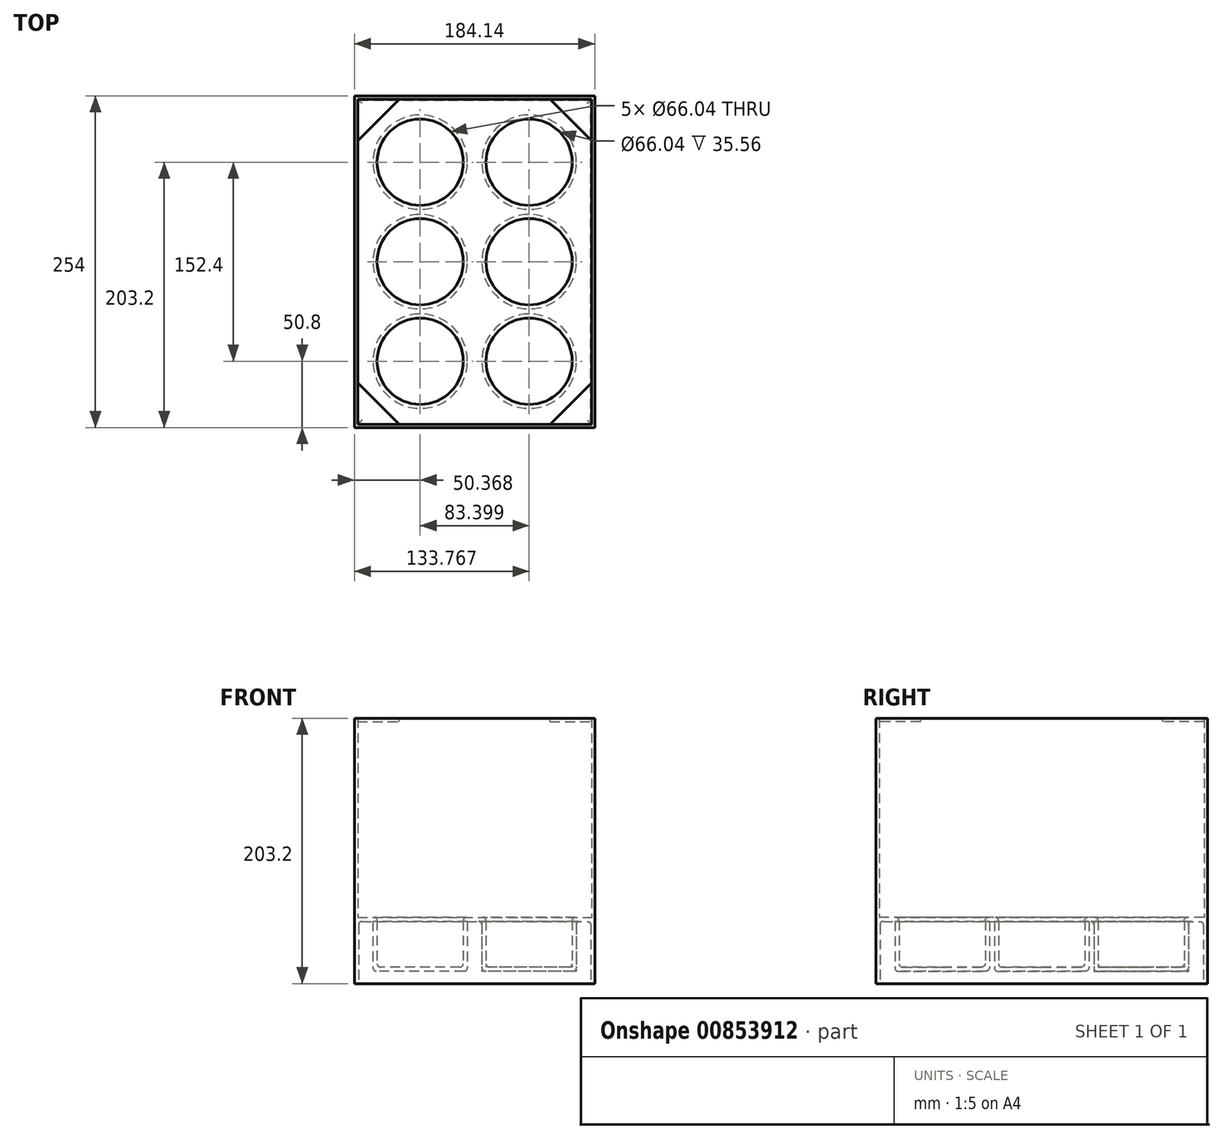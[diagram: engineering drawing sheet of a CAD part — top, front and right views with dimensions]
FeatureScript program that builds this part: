
annotation { "Feature Type Name" : "Feature", "Feature Type Description" : "" }
export const myFeature = defineFeature(function(context is Context, id is Id, definition is map)
    precondition{}
    {
        {
            var Q0;
            Q0=qCreatedBy(makeId("Top.planeOp"),FACE);
            var sketch = newSketch(context, id + "F0", { "sketchPlane" : qUnion([Q0])});
            skLineSegment(sketch, "E0.bottom", {"start": v(0, 0) * mm, "end": v(184.14, 0) * mm});
            skLineSegment(sketch, "E0.top", {"start": v(0, 254) * mm, "end": v(184.14, 254) * mm});
            skLineSegment(sketch, "E0.left", {"start": v(0, 0) * mm, "end": v(0, 254) * mm});
            skLineSegment(sketch, "E0.right", {"start": v(184.14, 0) * mm, "end": v(184.14, 254) * mm});
            skSolve(sketch);
        }
        {
            var Q0;
            Q0=makeQuery(id+"F0.imprint","IMPRINT",FACE,{"disambiguationData":[TD([[makeQuery(id+"F0.imprint","IMPRINT",EDGE,{"derivedFrom":sQuery(id+"F0.wireOp",EDGE,"E0.bottom")}),1.0]])]});
            extrude(context, id + "F1", {"entities" : qUnion([Q0]), "depth" : 12.7 * mm, "offsetDistance" : 25.4 * mm});
        }
        {
            var Q0;
            Q0=makeQuery(id+"F1.opExtrude","CAP_FACE",FACE,{"disambiguationData":[OSD([sQuery(id+"F0.wireOp",EDGE,"E0.bottom"),sQuery(id+"F0.wireOp",EDGE,"E0.top"),sQuery(id+"F0.wireOp",EDGE,"E0.left"),sQuery(id+"F0.wireOp",EDGE,"E0.right")])],"isStart":false});
            var sketch = newSketch(context, id + "F2", { "sketchPlane" : qUnion([Q0])});
            skCircle(sketch, "E1", {"center": v(50.37, 50.8) * mm, "radius": 33.02 * mm});
            skCircle(sketch, "E2", {"center": v(133.77, 50.8) * mm, "radius": 33.02 * mm});
            skCircle(sketch, "E3", {"center": v(50.37, 127) * mm, "radius": 33.02 * mm});
            skCircle(sketch, "E4", {"center": v(133.77, 127) * mm, "radius": 33.02 * mm});
            skCircle(sketch, "E5", {"center": v(50.37, 203.2) * mm, "radius": 33.02 * mm});
            skCircle(sketch, "E6", {"center": v(133.77, 203.2) * mm, "radius": 33.02 * mm});
            skSolve(sketch);
        }
        {
            var Q0;
            Q0=makeQuery(id+"F2.imprint","IMPRINT",FACE,{"disambiguationData":[TD([[makeQuery(id+"F2.imprint","IMPRINT",EDGE,{"derivedFrom":sQuery(id+"F2.wireOp",EDGE,"E1")}),-1.0]])]});
            extrude(context, id + "F3", {"entities" : qUnion([Q0]), "operationType" : NewBodyOperationType.ADD, "depth" : 38.1 * mm, "offsetDistance" : 25.4 * mm});
        }
        {
            var Q0;
            Q0=makeQuery(id+"F1.opExtrude","CAP_FACE",FACE,{"disambiguationData":[OSD([sQuery(id+"F0.wireOp",EDGE,"E0.bottom"),sQuery(id+"F0.wireOp",EDGE,"E0.top"),sQuery(id+"F0.wireOp",EDGE,"E0.left"),sQuery(id+"F0.wireOp",EDGE,"E0.right")])],"isStart":true});
            shell(context, id + "F4", {"entities" : qUnion([Q0]), "thickness" : 3.17 * mm});
        }
        {
            var Q0;
            Q0=makeQuery(id+"F3.opExtrude","CAP_EDGE",EDGE,{"disambiguationData":[OSD([sQuery(id+"F2.wireOp",EDGE,"E4")])],"isStart":true});
            var Q1;
            Q1=makeQuery(id+"F3.opExtrude","CAP_EDGE",EDGE,{"disambiguationData":[OSD([sQuery(id+"F2.wireOp",EDGE,"E6")])],"isStart":true});
            var Q2;
            Q2=makeQuery(id+"F3.opExtrude","CAP_EDGE",EDGE,{"disambiguationData":[OSD([sQuery(id+"F2.wireOp",EDGE,"E5")])],"isStart":true});
            var Q3;
            Q3=makeQuery(id+"F3.opExtrude","CAP_EDGE",EDGE,{"disambiguationData":[OSD([sQuery(id+"F2.wireOp",EDGE,"E3")])],"isStart":true});
            var Q4;
            Q4=makeQuery(id+"F3.opExtrude","CAP_EDGE",EDGE,{"disambiguationData":[OSD([sQuery(id+"F2.wireOp",EDGE,"E1")])],"isStart":true});
            var Q5;
            Q5=makeQuery(id+"F3.opExtrude","CAP_EDGE",EDGE,{"disambiguationData":[OSD([sQuery(id+"F2.wireOp",EDGE,"E2")])],"isStart":true});
            var Q6;
            Q6=makeQuery(id+"F3.opExtrude","CAP_EDGE",EDGE,{"disambiguationData":[OSD([sQuery(id+"F2.wireOp",EDGE,"E4")])],"isStart":false});
            var Q7;
            Q7=makeQuery(id+"F3.opExtrude","CAP_EDGE",EDGE,{"disambiguationData":[OSD([sQuery(id+"F2.wireOp",EDGE,"E6")])],"isStart":false});
            var Q8;
            Q8=makeQuery(id+"F3.opExtrude","CAP_EDGE",EDGE,{"disambiguationData":[OSD([sQuery(id+"F2.wireOp",EDGE,"E2")])],"isStart":false});
            var Q9;
            Q9=makeQuery(id+"F3.opExtrude","CAP_EDGE",EDGE,{"disambiguationData":[OSD([sQuery(id+"F2.wireOp",EDGE,"E1")])],"isStart":false});
            var Q10;
            Q10=makeQuery(id+"F3.opExtrude","CAP_EDGE",EDGE,{"disambiguationData":[OSD([sQuery(id+"F2.wireOp",EDGE,"E3")])],"isStart":false});
            var Q11;
            Q11=makeQuery(id+"F3.opExtrude","CAP_EDGE",EDGE,{"disambiguationData":[OSD([sQuery(id+"F2.wireOp",EDGE,"E5")])],"isStart":false});
            fillet(context, id + "F5", {"entities" : qUnion([Q0, Q1, Q2, Q3, Q4, Q5, Q6, Q7, Q8, Q9, Q10, Q11]), "radius" : 2.54 * mm, "tangentPropagation" : true, "allowEdgeOverflow" : false});
        }
        {
            var Q0;
            {var subQ0=sQuery(id+"F0.wireOp",EDGE,"E0.top");Q0=makeQuery(id+"F4.opShell","OFFSET_EDGE",EDGE,{"disambiguationData":[OSD([subQ0]),TDD([makeQuery(id+"F3.opExtrude","CAP_EDGE",EDGE,{"disambiguationData":[OSD([subQ0])],"isStart":false})])]});}
            var Q1;
            {var subQ0=sQuery(id+"F0.wireOp",EDGE,"E0.right");Q1=makeQuery(id+"F4.opShell","OFFSET_EDGE",EDGE,{"disambiguationData":[OSD([subQ0]),TDD([makeQuery(id+"F3.opExtrude","CAP_EDGE",EDGE,{"disambiguationData":[OSD([subQ0])],"isStart":false})])]});}
            var Q2;
            {var subQ0=sQuery(id+"F0.wireOp",EDGE,"E0.bottom");Q2=makeQuery(id+"F4.opShell","OFFSET_EDGE",EDGE,{"disambiguationData":[OSD([subQ0]),TDD([makeQuery(id+"F3.opExtrude","CAP_EDGE",EDGE,{"disambiguationData":[OSD([subQ0])],"isStart":false})])]});}
            var Q3;
            {var subQ0=sQuery(id+"F0.wireOp",EDGE,"E0.left");Q3=makeQuery(id+"F4.opShell","OFFSET_EDGE",EDGE,{"disambiguationData":[OSD([subQ0]),TDD([makeQuery(id+"F3.opExtrude","CAP_EDGE",EDGE,{"disambiguationData":[OSD([subQ0])],"isStart":false})])]});}
            var Q4;
            {var subQ0=sQuery(id+"F2.wireOp",EDGE,"E2");Q4=makeQuery(id+"F4.opShell","OFFSET_EDGE",EDGE,{"disambiguationData":[OSD([subQ0]),TDD([makeQuery(id+"F3.opExtrude","CAP_EDGE",EDGE,{"disambiguationData":[OSD([subQ0])],"isStart":true})])]});}
            var Q5;
            {var subQ0=sQuery(id+"F2.wireOp",EDGE,"E4");Q5=makeQuery(id+"F4.opShell","OFFSET_EDGE",EDGE,{"disambiguationData":[OSD([subQ0]),TDD([makeQuery(id+"F3.opExtrude","CAP_EDGE",EDGE,{"disambiguationData":[OSD([subQ0])],"isStart":true})])]});}
            var Q6;
            {var subQ0=sQuery(id+"F2.wireOp",EDGE,"E6");Q6=makeQuery(id+"F4.opShell","OFFSET_EDGE",EDGE,{"disambiguationData":[OSD([subQ0]),TDD([makeQuery(id+"F3.opExtrude","CAP_EDGE",EDGE,{"disambiguationData":[OSD([subQ0])],"isStart":true})])]});}
            var Q7;
            {var subQ0=sQuery(id+"F2.wireOp",EDGE,"E5");Q7=makeQuery(id+"F4.opShell","OFFSET_EDGE",EDGE,{"disambiguationData":[OSD([subQ0]),TDD([makeQuery(id+"F3.opExtrude","CAP_EDGE",EDGE,{"disambiguationData":[OSD([subQ0])],"isStart":true})])]});}
            var Q8;
            {var subQ0=sQuery(id+"F2.wireOp",EDGE,"E3");Q8=makeQuery(id+"F4.opShell","OFFSET_EDGE",EDGE,{"disambiguationData":[OSD([subQ0]),TDD([makeQuery(id+"F3.opExtrude","CAP_EDGE",EDGE,{"disambiguationData":[OSD([subQ0])],"isStart":true})])]});}
            var Q9;
            {var subQ0=sQuery(id+"F2.wireOp",EDGE,"E1");Q9=makeQuery(id+"F4.opShell","OFFSET_EDGE",EDGE,{"disambiguationData":[OSD([subQ0]),TDD([makeQuery(id+"F3.opExtrude","CAP_EDGE",EDGE,{"disambiguationData":[OSD([subQ0])],"isStart":true})])]});}
            fillet(context, id + "F6", {"entities" : qUnion([Q0, Q1, Q2, Q3, Q4, Q5, Q6, Q7, Q8, Q9]), "radius" : 2.54 * mm, "tangentPropagation" : true, "allowEdgeOverflow" : false});
        }
        {
            var Q0;
            Q0=makeQuery(id+"F3.opExtrude","CAP_FACE",FACE,{"disambiguationData":[OSD([sQuery(id+"F0.wireOp",EDGE,"E0.bottom"),sQuery(id+"F0.wireOp",EDGE,"E0.top"),sQuery(id+"F0.wireOp",EDGE,"E0.left"),sQuery(id+"F0.wireOp",EDGE,"E0.right"),sQuery(id+"F2.wireOp",EDGE,"E1"),sQuery(id+"F2.wireOp",EDGE,"E2"),sQuery(id+"F2.wireOp",EDGE,"E3"),sQuery(id+"F2.wireOp",EDGE,"E4"),sQuery(id+"F2.wireOp",EDGE,"E5"),sQuery(id+"F2.wireOp",EDGE,"E6")])],"isStart":false});
            var sketch = newSketch(context, id + "F7", { "sketchPlane" : qUnion([Q0])});
            skLineSegment(sketch, "E7.bottom", {"start": v(0, 254) * mm, "end": v(184.14, 254) * mm});
            skLineSegment(sketch, "E7.top", {"start": v(0, 0) * mm, "end": v(184.14, 0) * mm});
            skLineSegment(sketch, "E7.left", {"start": v(0, 254) * mm, "end": v(0, 0) * mm});
            skLineSegment(sketch, "E7.right", {"start": v(184.14, 254) * mm, "end": v(184.14, 0) * mm});
            skLineSegment(sketch, "E8.bottom", {"start": v(2.54, 251.46) * mm, "end": v(181.6, 251.46) * mm});
            skLineSegment(sketch, "E8.top", {"start": v(2.54, 2.54) * mm, "end": v(181.6, 2.54) * mm});
            skLineSegment(sketch, "E8.left", {"start": v(2.54, 251.46) * mm, "end": v(2.54, 2.54) * mm});
            skLineSegment(sketch, "E8.right", {"start": v(181.6, 251.46) * mm, "end": v(181.6, 2.54) * mm});
            skSolve(sketch);
        }
        {
            var Q0;
            Q0=makeQuery(id+"F7.imprint","IMPRINT",FACE,{"disambiguationData":[TD([[makeQuery(id+"F7.imprint","IMPRINT",EDGE,{"derivedFrom":sQuery(id+"F7.wireOp",EDGE,"E7.bottom")}),-1.0]])]});
            extrude(context, id + "F8", {"entities" : qUnion([Q0]), "operationType" : NewBodyOperationType.ADD, "depth" : 152.4 * mm, "offsetDistance" : 25.4 * mm});
        }
        {
            var Q0;
            Q0=makeQuery(id+"F8.opExtrude","CAP_FACE",FACE,{"disambiguationData":[OSD([sQuery(id+"F7.wireOp",EDGE,"E7.bottom"),sQuery(id+"F7.wireOp",EDGE,"E7.top"),sQuery(id+"F7.wireOp",EDGE,"E7.left"),sQuery(id+"F7.wireOp",EDGE,"E7.right"),sQuery(id+"F7.wireOp",EDGE,"E8.bottom"),sQuery(id+"F7.wireOp",EDGE,"E8.top"),sQuery(id+"F7.wireOp",EDGE,"E8.left"),sQuery(id+"F7.wireOp",EDGE,"E8.right")])],"isStart":false});
            var sketch = newSketch(context, id + "F9", { "sketchPlane" : qUnion([Q0])});
            skLineSegment(sketch, "E9", {"start": v(2.54, 251.46) * mm, "end": v(2.54, 219.71) * mm});
            skLineSegment(sketch, "E10", {"start": v(2.54, 219.71) * mm, "end": v(34.3, 251.46) * mm});
            skLineSegment(sketch, "E11", {"start": v(34.3, 251.46) * mm, "end": v(2.54, 251.46) * mm});
            skLineSegment(sketch, "E12", {"start": v(181.6, 251.46) * mm, "end": v(149.85, 251.46) * mm});
            skLineSegment(sketch, "E13", {"start": v(149.85, 251.46) * mm, "end": v(181.6, 219.71) * mm});
            skLineSegment(sketch, "E14", {"start": v(181.6, 219.71) * mm, "end": v(181.6, 251.46) * mm});
            skLineSegment(sketch, "E15", {"start": v(2.54, 2.54) * mm, "end": v(2.54, 34.3) * mm});
            skLineSegment(sketch, "E16", {"start": v(2.54, 34.3) * mm, "end": v(34.3, 2.54) * mm});
            skLineSegment(sketch, "E17", {"start": v(181.6, 2.54) * mm, "end": v(149.85, 2.54) * mm});
            skLineSegment(sketch, "E18", {"start": v(149.85, 2.54) * mm, "end": v(181.6, 34.3) * mm});
            skLineSegment(sketch, "E19", {"start": v(181.6, 34.3) * mm, "end": v(181.6, 2.54) * mm});
            skLineSegment(sketch, "E20", {"start": v(2.54, 2.54) * mm, "end": v(34.3, 2.54) * mm});
            skSolve(sketch);
        }
        {
            var Q0;
            Q0=makeQuery(id+"F9.imprint","IMPRINT",FACE,{"disambiguationData":[TD([[makeQuery(id+"F9.imprint","IMPRINT",EDGE,{"derivedFrom":sQuery(id+"F9.wireOp",EDGE,"E9")}),1.0]])]});
            var Q1;
            Q1=makeQuery(id+"F9.imprint","IMPRINT",FACE,{"disambiguationData":[TD([[makeQuery(id+"F9.imprint","IMPRINT",EDGE,{"derivedFrom":sQuery(id+"F9.wireOp",EDGE,"E15")}),1.0]])]});
            var Q2;
            Q2=makeQuery(id+"F9.imprint","IMPRINT",FACE,{"disambiguationData":[TD([[makeQuery(id+"F9.imprint","IMPRINT",EDGE,{"derivedFrom":sQuery(id+"F9.wireOp",EDGE,"E17")}),1.0]])]});
            var Q3;
            Q3=makeQuery(id+"F9.imprint","IMPRINT",FACE,{"disambiguationData":[TD([[makeQuery(id+"F9.imprint","IMPRINT",EDGE,{"derivedFrom":sQuery(id+"F9.wireOp",EDGE,"E12")}),-1.0]])]});
            extrude(context, id + "F10", {"entities" : qUnion([Q0, Q1, Q2, Q3]), "oppositeDirection" : true, "depth" : 2.54 * mm, "offsetDistance" : 25.4 * mm});
        }
    });
